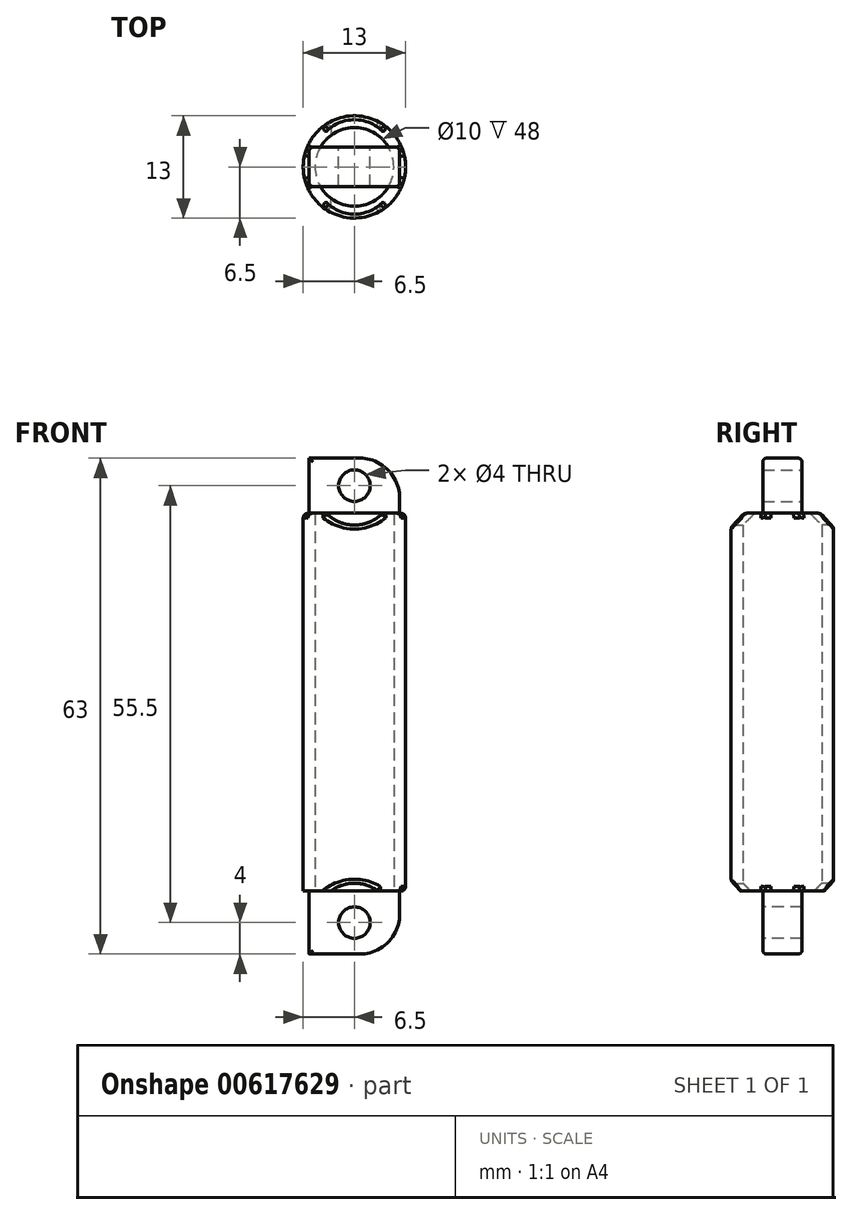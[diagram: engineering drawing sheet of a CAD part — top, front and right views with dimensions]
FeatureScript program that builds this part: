
annotation { "Feature Type Name" : "Feature", "Feature Type Description" : "" }
export const myFeature = defineFeature(function(context is Context, id is Id, definition is map)
    precondition{}
    {
        {
            var Q0;
            Q0=qCreatedBy(makeId("Top.planeOp"),FACE);
            var sketch = newSketch(context, id + "F0", { "sketchPlane" : qUnion([Q0])});
            skCircle(sketch, "E0", {"center": v(0, 0) * mm, "radius": 6.5 * mm});
            skSolve(sketch);
        }
        {
            var Q0;
            Q0=qSketchRegion(id+"F0",true);
            extrude(context, id + "F1", {"entities" : qUnion([Q0]), "depth" : 48 * mm, "offsetDistance" : 25 * mm});
        }
        {
            var Q0;
            Q0=qCreatedBy(makeId("Top.planeOp"),FACE);
            var sketch = newSketch(context, id + "F2", { "sketchPlane" : qUnion([Q0])});
            skLineSegment(sketch, "E1.bottom", {"start": v(5.75, 2.5) * mm, "end": v(-5.75, 2.5) * mm});
            skLineSegment(sketch, "E1.top", {"start": v(5.75, -2.5) * mm, "end": v(-5.75, -2.5) * mm});
            skLineSegment(sketch, "E1.left", {"start": v(5.75, 2.5) * mm, "end": v(5.75, -2.5) * mm});
            skLineSegment(sketch, "E1.right", {"start": v(-5.75, 2.5) * mm, "end": v(-5.75, -2.5) * mm});
            skPoint(sketch, "E1.middle", {"position": v(0, 0) * mm});
            skSolve(sketch);
        }
        {
            var Q0;
            Q0=makeQuery(id+"F1.opExtrude","CAP_FACE",FACE,{"disambiguationData":[OSD([sQuery(id+"F0.wireOp",EDGE,"E0")])],"isStart":false});
            var Q1;
            Q1=makeQuery(id+"F1.opExtrude","CAP_FACE",FACE,{"disambiguationData":[OSD([sQuery(id+"F0.wireOp",EDGE,"E0")])],"isStart":true});
            shell(context, id + "F3", {"entities" : qUnion([Q0, Q1]), "thickness" : 1.5 * mm});
        }
        {
            var Q0;
            Q0=qSketchRegion(id+"F2",true);
            extrude(context, id + "F4", {"entities" : qUnion([Q0]), "operationType" : NewBodyOperationType.ADD, "oppositeDirection" : true, "depth" : 8 * mm, "offsetDistance" : 25 * mm});
        }
        {
            var Q0;
            Q0=makeQuery(id+"F1.opExtrude","CAP_FACE",FACE,{"disambiguationData":[OSD([sQuery(id+"F0.wireOp",EDGE,"E0")])],"isStart":false});
            var sketch = newSketch(context, id + "F5", { "sketchPlane" : qUnion([Q0])});
            skLineSegment(sketch, "E2.bottom", {"start": v(5.75, 2.5) * mm, "end": v(-5.75, 2.5) * mm});
            skLineSegment(sketch, "E2.top", {"start": v(5.75, -2.5) * mm, "end": v(-5.75, -2.5) * mm});
            skLineSegment(sketch, "E2.left", {"start": v(5.75, 2.5) * mm, "end": v(5.75, -2.5) * mm});
            skLineSegment(sketch, "E2.right", {"start": v(-5.75, 2.5) * mm, "end": v(-5.75, -2.5) * mm});
            skPoint(sketch, "E2.middle", {"position": v(0, 0) * mm});
            skSolve(sketch);
        }
        {
            var Q0;
            Q0=qSketchRegion(id+"F5",true);
            extrude(context, id + "F6", {"entities" : qUnion([Q0]), "operationType" : NewBodyOperationType.ADD, "depth" : 7 * mm, "offsetDistance" : 25 * mm});
        }
        {
            var Q0;
            Q0=makeQuery(id+"F6.opExtrude","SWEPT_FACE",FACE,{"disambiguationData":[OSD([sQuery(id+"F5.wireOp",EDGE,"E2.bottom")])]});
            var sketch = newSketch(context, id + "F7", { "sketchPlane" : qUnion([Q0])});
            skCircle(sketch, "E3", {"center": v(0, 51.5) * mm, "radius": 2 * mm});
            skPoint(sketch, "E3.centerSnap0", {"position": v(-5.75, 51.5) * mm});
            skSolve(sketch);
        }
        {
            var Q0;
            Q0=qSketchRegion(id+"F7",true);
            extrude(context, id + "F8", {"entities" : qUnion([Q0]), "operationType" : NewBodyOperationType.REMOVE, "oppositeDirection" : true, "depth" : 5 * mm, "offsetDistance" : 25 * mm});
        }
        {
            var Q0;
            Q0=makeQuery(id+"F4.opExtrude","SWEPT_FACE",FACE,{"disambiguationData":[OSD([sQuery(id+"F2.wireOp",EDGE,"E1.top")])]});
            var sketch = newSketch(context, id + "F9", { "sketchPlane" : qUnion([Q0])});
            skCircle(sketch, "E4", {"center": v(0, -4) * mm, "radius": 2 * mm});
            skPoint(sketch, "E4.centerSnap0", {"position": v(-5.75, -4) * mm});
            skSolve(sketch);
        }
        {
            var Q0;
            Q0=qSketchRegion(id+"F9",true);
            extrude(context, id + "F10", {"entities" : qUnion([Q0]), "operationType" : NewBodyOperationType.REMOVE, "oppositeDirection" : true, "depth" : 5 * mm, "offsetDistance" : 25 * mm});
        }
        {
            var Q0;
            Q0=makeQuery(id+"F4.opExtrude","CAP_EDGE",EDGE,{"disambiguationData":[OSD([sQuery(id+"F2.wireOp",EDGE,"E1.left")])],"isStart":false});
            var Q1;
            Q1=makeQuery(id+"F6.opExtrude","CAP_EDGE",EDGE,{"disambiguationData":[OSD([sQuery(id+"F5.wireOp",EDGE,"E2.left")])],"isStart":false});
            fillet(context, id + "F11", {"entities" : qUnion([Q0, Q1]), "radius" : 5 * mm, "tangentPropagation" : true, "rho" : 0.4, "crossSection" : FilletCrossSection.CONIC, "allowEdgeOverflow" : false});
        }
        {
            var Q0;
            Q0=makeQuery(id+"F6.opExtrude","SWEPT_EDGE",EDGE,{"disambiguationData":[OSD([sQuery(id+"F5.wireOp",EDGE,"E2.top"),sQuery(id+"F5.wireOp",EDGE,"E2.right")])]});
            var Q1;
            Q1=makeQuery(id+"F6.opExtrude","SWEPT_EDGE",EDGE,{"disambiguationData":[OSD([sQuery(id+"F5.wireOp",EDGE,"E2.bottom"),sQuery(id+"F5.wireOp",EDGE,"E2.right")])]});
            var Q2;
            Q2=makeQuery(id+"F11.opFillet","BLEND_EDGE",EDGE,{"blendedFrom":[makeQuery(id+"F6.opExtrude","CAP_EDGE",EDGE,{"disambiguationData":[OSD([sQuery(id+"F5.wireOp",EDGE,"E2.left")])],"isStart":false}),makeQuery(id+"F6.opExtrude","SWEPT_FACE",FACE,{"disambiguationData":[OSD([sQuery(id+"F5.wireOp",EDGE,"E2.bottom")])]})],"blendedInto":[makeQuery(id+"F6.opExtrude","SWEPT_FACE",FACE,{"disambiguationData":[OSD([sQuery(id+"F5.wireOp",EDGE,"E2.bottom")])]})]});
            var Q3;
            Q3=makeQuery(id+"F11.opFillet","BLEND_EDGE",EDGE,{"blendedFrom":[makeQuery(id+"F6.opExtrude","CAP_EDGE",EDGE,{"disambiguationData":[OSD([sQuery(id+"F5.wireOp",EDGE,"E2.left")])],"isStart":false}),makeQuery(id+"F6.opExtrude","SWEPT_FACE",FACE,{"disambiguationData":[OSD([sQuery(id+"F5.wireOp",EDGE,"E2.top")])]})],"blendedInto":[makeQuery(id+"F6.opExtrude","SWEPT_FACE",FACE,{"disambiguationData":[OSD([sQuery(id+"F5.wireOp",EDGE,"E2.top")])]})]});
            var Q4;
            Q4=makeQuery(id+"F4.opExtrude","SWEPT_EDGE",EDGE,{"disambiguationData":[OSD([sQuery(id+"F2.wireOp",EDGE,"E1.top"),sQuery(id+"F2.wireOp",EDGE,"E1.right")])]});
            var Q5;
            Q5=makeQuery(id+"F4.opExtrude","SWEPT_EDGE",EDGE,{"disambiguationData":[OSD([sQuery(id+"F2.wireOp",EDGE,"E1.bottom"),sQuery(id+"F2.wireOp",EDGE,"E1.right")])]});
            var Q6;
            Q6=makeQuery(id+"F4.opExtrude","CAP_EDGE",EDGE,{"disambiguationData":[OSD([sQuery(id+"F2.wireOp",EDGE,"E1.top")])],"isStart":false});
            var Q7;
            Q7=makeQuery(id+"F11.opFillet","BLEND_EDGE",EDGE,{"blendedFrom":[makeQuery(id+"F4.opExtrude","CAP_EDGE",EDGE,{"disambiguationData":[OSD([sQuery(id+"F2.wireOp",EDGE,"E1.left")])],"isStart":false}),makeQuery(id+"F4.opExtrude","SWEPT_FACE",FACE,{"disambiguationData":[OSD([sQuery(id+"F2.wireOp",EDGE,"E1.bottom")])]})],"blendedInto":[makeQuery(id+"F4.opExtrude","SWEPT_FACE",FACE,{"disambiguationData":[OSD([sQuery(id+"F2.wireOp",EDGE,"E1.bottom")])]})]});
            fillet(context, id + "F12", {"entities" : qUnion([Q0, Q1, Q2, Q3, Q4, Q5, Q6, Q7]), "radius" : 0.5 * mm, "tangentPropagation" : true, "allowEdgeOverflow" : false});
        }
        {
            var Q0;
            Q0=makeQuery(id+"F6.opExtrude","SWEPT_FACE",FACE,{"disambiguationData":[OSD([sQuery(id+"F5.wireOp",EDGE,"E2.top")])]});
            var sketch = newSketch(context, id + "F13", { "sketchPlane" : qUnion([Q0])});
            skCircle(sketch, "E5", {"center": v(0, 51.5) * mm, "radius": 5 * mm});
            skSolve(sketch);
        }
        {
            var Q0;
            Q0=qSketchRegion(id+"F13",true);
            extrude(context, id + "F14", {"entities" : qUnion([Q0]), "operationType" : NewBodyOperationType.REMOVE, "depth" : 5 * mm, "offsetDistance" : 25 * mm});
        }
        {
            var Q0;
            Q0=makeQuery(id+"F6.opExtrude","SWEPT_FACE",FACE,{"disambiguationData":[OSD([sQuery(id+"F5.wireOp",EDGE,"E2.bottom")])]});
            var sketch = newSketch(context, id + "F15", { "sketchPlane" : qUnion([Q0])});
            skCircle(sketch, "E6", {"center": v(0, 51.5) * mm, "radius": 5 * mm});
            skSolve(sketch);
        }
        {
            var Q0;
            Q0=qSketchRegion(id+"F15",true);
            extrude(context, id + "F16", {"entities" : qUnion([Q0]), "operationType" : NewBodyOperationType.REMOVE, "depth" : 5 * mm, "offsetDistance" : 25 * mm});
        }
        {
            var Q0;
            Q0=makeQuery(id+"F4.opExtrude","SWEPT_FACE",FACE,{"disambiguationData":[OSD([sQuery(id+"F2.wireOp",EDGE,"E1.top")])]});
            var sketch = newSketch(context, id + "F17", { "sketchPlane" : qUnion([Q0])});
            skCircle(sketch, "E7", {"center": v(0, -4) * mm, "radius": 5 * mm});
            skSolve(sketch);
        }
        {
            var Q0;
            Q0=qSketchRegion(id+"F17",true);
            extrude(context, id + "F18", {"entities" : qUnion([Q0]), "operationType" : NewBodyOperationType.REMOVE, "depth" : 5 * mm, "offsetDistance" : 25 * mm});
        }
        {
            var Q0;
            Q0=makeQuery(id+"F4.opExtrude","SWEPT_FACE",FACE,{"disambiguationData":[OSD([sQuery(id+"F2.wireOp",EDGE,"E1.bottom")])]});
            var sketch = newSketch(context, id + "F19", { "sketchPlane" : qUnion([Q0])});
            skCircle(sketch, "E8", {"center": v(0, -4) * mm, "radius": 5 * mm});
            skSolve(sketch);
        }
        {
            var Q0;
            Q0=qSketchRegion(id+"F19",true);
            extrude(context, id + "F20", {"entities" : qUnion([Q0]), "operationType" : NewBodyOperationType.REMOVE, "depth" : 5 * mm, "offsetDistance" : 25 * mm});
        }
        {
            var Q0;
            Q0=makeQuery(id+"F16.boolean.opBoolean","SPLIT",EDGE,{"disambiguationData":[OD(0.0)],"derivedFrom":makeQuery(id+"F1.opExtrude","CAP_EDGE",EDGE,{"disambiguationData":[OSD([sQuery(id+"F0.wireOp",EDGE,"E0")])],"isStart":false})});
            var Q1;
            Q1=makeQuery(id+"F16.boolean.opBoolean","SPLIT",EDGE,{"disambiguationData":[OD(1.0)],"derivedFrom":makeQuery(id+"F1.opExtrude","CAP_EDGE",EDGE,{"disambiguationData":[OSD([sQuery(id+"F0.wireOp",EDGE,"E0")])],"isStart":false})});
            var Q2;
            Q2=makeQuery(id+"F20.boolean.opBoolean","SPLIT",EDGE,{"disambiguationData":[OD(0.0)],"derivedFrom":makeQuery(id+"F1.opExtrude","CAP_EDGE",EDGE,{"disambiguationData":[OSD([sQuery(id+"F0.wireOp",EDGE,"E0")])],"isStart":true})});
            fillet(context, id + "F21", {"entities" : qUnion([Q0, Q1, Q2]), "radius" : 0.6 * mm, "tangentPropagation" : true, "allowEdgeOverflow" : false});
        }
        {
            var Q0;
            Q0=makeQuery(id+"F20.boolean.opBoolean","INTERSECT",EDGE,{"derivedFrom":[makeQuery(id+"F1.opExtrude","SWEPT_FACE",FACE,{"disambiguationData":[OSD([sQuery(id+"F0.wireOp",EDGE,"E0")])]}),makeQuery(id+"F20.opExtrude","SWEPT_FACE",FACE,{"disambiguationData":[OSD([sQuery(id+"F19.wireOp",EDGE,"E8")])]})]});
            var Q1;
            Q1=makeQuery(id+"F16.boolean.opBoolean","INTERSECT",EDGE,{"derivedFrom":[makeQuery(id+"F1.opExtrude","SWEPT_FACE",FACE,{"disambiguationData":[OSD([sQuery(id+"F0.wireOp",EDGE,"E0")])]}),makeQuery(id+"F16.opExtrude","SWEPT_FACE",FACE,{"disambiguationData":[OSD([sQuery(id+"F15.wireOp",EDGE,"E6")])]})]});
            var Q2;
            Q2=makeQuery(id+"F14.boolean.opBoolean","INTERSECT",EDGE,{"derivedFrom":[makeQuery(id+"F1.opExtrude","SWEPT_FACE",FACE,{"disambiguationData":[OSD([sQuery(id+"F0.wireOp",EDGE,"E0")])]}),makeQuery(id+"F14.opExtrude","SWEPT_FACE",FACE,{"disambiguationData":[OSD([sQuery(id+"F13.wireOp",EDGE,"E5")])]})]});
            var Q3;
            Q3=makeQuery(id+"F18.boolean.opBoolean","INTERSECT",EDGE,{"derivedFrom":[makeQuery(id+"F1.opExtrude","SWEPT_FACE",FACE,{"disambiguationData":[OSD([sQuery(id+"F0.wireOp",EDGE,"E0")])]}),makeQuery(id+"F18.opExtrude","SWEPT_FACE",FACE,{"disambiguationData":[OSD([sQuery(id+"F17.wireOp",EDGE,"E7")])]})]});
            fillet(context, id + "F22", {"entities" : qUnion([Q0, Q1, Q2, Q3]), "radius" : 0.5 * mm, "tangentPropagation" : true, "allowEdgeOverflow" : false});
        }
    });
